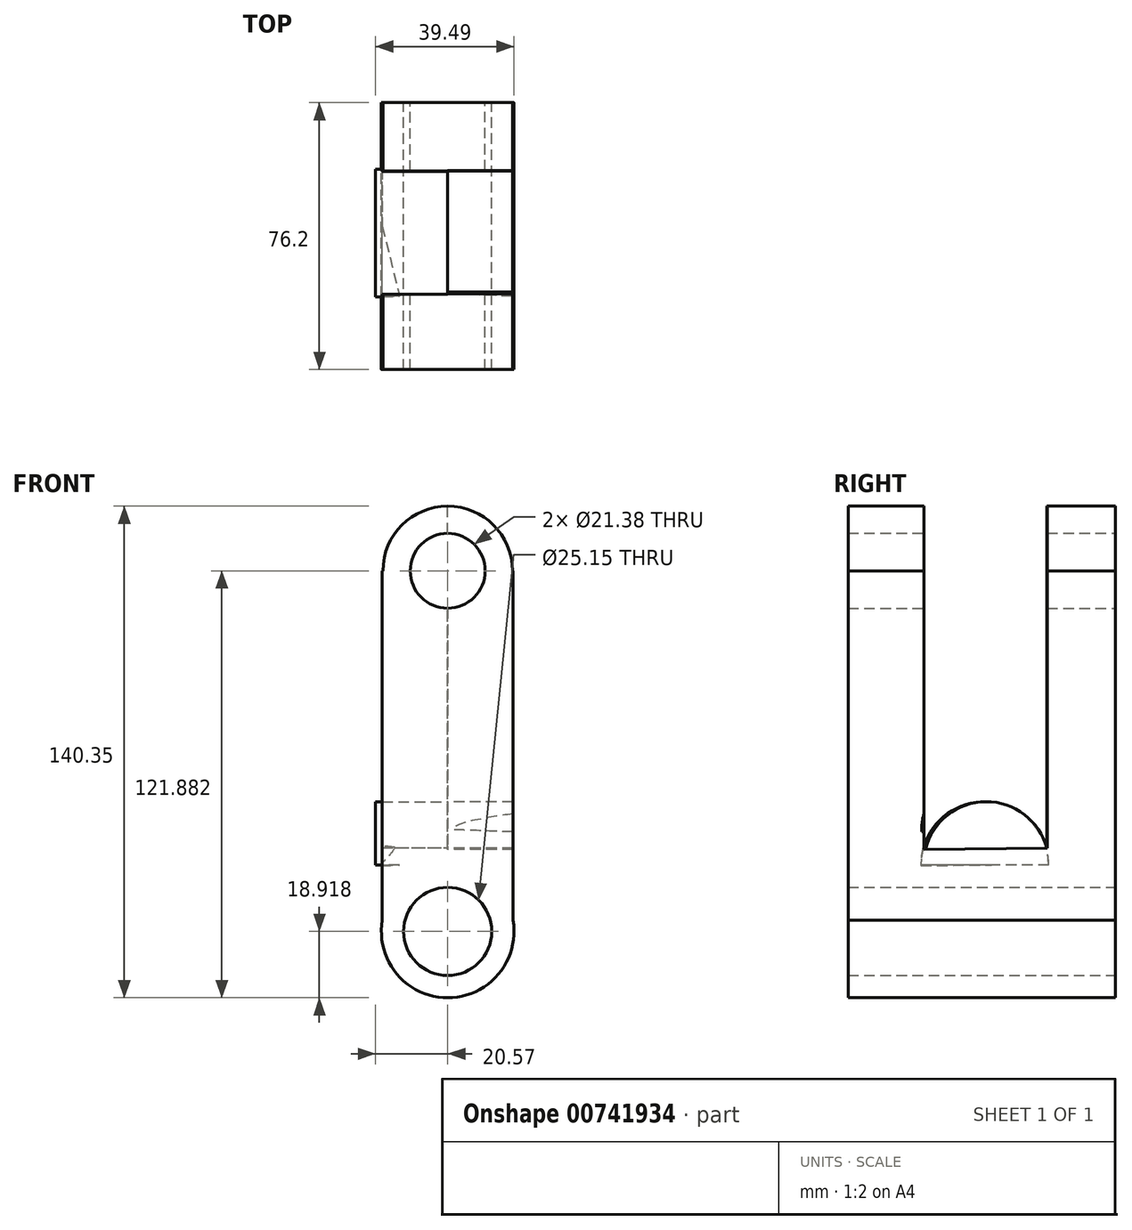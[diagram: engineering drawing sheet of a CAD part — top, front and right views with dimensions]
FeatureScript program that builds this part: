
annotation { "Feature Type Name" : "Feature", "Feature Type Description" : "" }
export const myFeature = defineFeature(function(context is Context, id is Id, definition is map)
    precondition{}
    {
        {
            var Q0;
            Q0=qCreatedBy(makeId("Front.planeOp"),FACE);
            var sketch = newSketch(context, id + "F0", { "sketchPlane" : qUnion([Q0])});
            skLineSegment(sketch, "E0.bottom", {"start": v(18.64, 51.48) * mm, "end": v(18.46, 51.48) * mm});
            skLineSegment(sketch, "E0.left", {"start": v(18.64, 51.48) * mm, "end": v(18.64, -51.48) * mm});
            skLineSegment(sketch, "E0.right", {"start": v(-18.64, 51.48) * mm, "end": v(-18.64, -51.48) * mm});
            skPoint(sketch, "E0.middle", {"position": v(0, 0) * mm});
            skArc(sketch, "E1", {"start": v(18.46, 51.48) * mm, "mid": v(0, 69.95) * mm, "end": v(-18.46, 51.48) * mm});
            skCircle(sketch, "E2", {"center": v(0, 51.48) * mm, "radius": 10.7 * mm});
            skArc(sketch, "E3", {"start": v(-18.64, -48.27) * mm, "mid": v(0, -70.4) * mm, "end": v(18.64, -48.27) * mm});
            skCircle(sketch, "E4", {"center": v(0, -51.48) * mm, "radius": 12.57 * mm});
            skLineSegment(sketch, "E5.trimOffspring", {"start": v(-18.46, 51.48) * mm, "end": v(-18.64, 51.48) * mm});
            skSolve(sketch);
        }
        {
            var Q0;
            {var subQ4=sQuery(id+"F0.wireOp",EDGE,"E0.bottom");Q0=makeQuery(id+"F0.imprint","IMPRINT",FACE,{"disambiguationData":[TD([[makeQuery(id+"F0.imprint","IMPRINT",EDGE,{"derivedFrom":subQ4}),1.0]])]});}
            extrude(context, id + "F1", {"entities" : qUnion([Q0]), "depth" : 76.2 * mm, "offsetDistance" : 25.4 * mm, "symmetric" : true});
        }
        {
            var Q0;
            Q0=qCreatedBy(makeId("Right.planeOp"),FACE);
            var sketch = newSketch(context, id + "F2", { "sketchPlane" : qUnion([Q0])});
            skArc(sketch, "E6", {"start": v(0, -15.34) * mm, "mid": v(11.68, -20.12) * mm, "end": v(16.65, -31.71) * mm});
            skArc(sketch, "E7", {"start": v(0, -15.34) * mm, "mid": v(-11.78, -20.22) * mm, "end": v(-16.66, -32) * mm});
            skLineSegment(sketch, "E8", {"start": v(16.65, -31.71) * mm, "end": v(-16.66, -32) * mm});
            skSolve(sketch);
        }
        {
            var Q0;
            Q0 = qSketchRegion(id + "F2", true);
            extrude(context, id + "F3", {"entities" : qUnion([Q0]), "operationType" : NewBodyOperationType.REMOVE, "oppositeDirection" : true, "depth" : 76.2 * mm, "offsetDistance" : 25.4 * mm, "hasDraft" : true, "draftAngle" : 2 * degree});
        }
        {
            var Q0;
            Q0=qCreatedBy(makeId("Right.planeOp"),FACE);
            var sketch = newSketch(context, id + "F4", { "sketchPlane" : qUnion([Q0])});
            skArc(sketch, "E9", {"start": v(0, -5.95) * mm, "mid": v(-11.61, -10.76) * mm, "end": v(-16.42, -22.38) * mm});
            skArc(sketch, "E10", {"start": v(0, -5.95) * mm, "mid": v(11.61, -10.76) * mm, "end": v(16.42, -22.38) * mm});
            skLineSegment(sketch, "E11", {"start": v(-16.42, -22.38) * mm, "end": v(16.42, -22.38) * mm});
            skSolve(sketch);
        }
        {
            var Q0;
            Q0 = qSketchRegion(id + "F4", true);
            extrude(context, id + "F5", {"entities" : qUnion([Q0]), "operationType" : NewBodyOperationType.REMOVE, "depth" : 76.2 * mm, "offsetDistance" : 25.4 * mm, "hasDraft" : true, "draftAngle" : 2 * degree});
        }
        {
            var Q0;
            Q0=qCreatedBy(makeId("Right.planeOp"),FACE);
            var sketch = newSketch(context, id + "F6", { "sketchPlane" : qUnion([Q0])});
            skLineSegment(sketch, "E12", {"start": v(-16.58, -27.52) * mm, "end": v(-16.58, 70.15) * mm});
            skLineSegment(sketch, "E13", {"start": v(-16.58, 70.15) * mm, "end": v(18.62, 70.15) * mm});
            skLineSegment(sketch, "E14", {"start": v(18.62, 70.15) * mm, "end": v(18.62, -27.52) * mm});
            skLineSegment(sketch, "E15", {"start": v(18.62, -27.52) * mm, "end": v(-16.58, -27.52) * mm});
            skSolve(sketch);
        }
        {
            var Q0;
            Q0 = qSketchRegion(id + "F6", true);
            extrude(context, id + "F7", {"entities" : qUnion([Q0]), "operationType" : NewBodyOperationType.REMOVE, "oppositeDirection" : true, "depth" : 76.2 * mm, "offsetDistance" : 25.4 * mm});
        }
        {
            var Q0;
            Q0=qCreatedBy(makeId("Right.planeOp"),FACE);
            var sketch = newSketch(context, id + "F8", { "sketchPlane" : qUnion([Q0])});
            skLineSegment(sketch, "E16", {"start": v(-16.47, -28) * mm, "end": v(-16.47, 70.08) * mm});
            skLineSegment(sketch, "E17", {"start": v(-16.47, 70.08) * mm, "end": v(18.71, 70.08) * mm});
            skLineSegment(sketch, "E18", {"start": v(18.71, 70.08) * mm, "end": v(18.71, -27.73) * mm});
            skLineSegment(sketch, "E19", {"start": v(18.71, -27.73) * mm, "end": v(-16.47, -28) * mm});
            skSolve(sketch);
        }
        {
            var Q0;
            Q0 = qSketchRegion(id + "F8", true);
            extrude(context, id + "F9", {"entities" : qUnion([Q0]), "operationType" : NewBodyOperationType.REMOVE, "depth" : 76.2 * mm, "offsetDistance" : 25.4 * mm});
        }
        {
            var Q0;
            Q0=qCreatedBy(makeId("Right.planeOp"),FACE);
            var sketch = newSketch(context, id + "F10", { "sketchPlane" : qUnion([Q0])});
            skArc(sketch, "E20", {"start": v(18.97, -29.4) * mm, "mid": v(1.1, -14.44) * mm, "end": v(-16.33, -29.9) * mm});
            skLineSegment(sketch, "E21", {"start": v(-16.33, -29.9) * mm, "end": v(18.97, -29.4) * mm});
            skSolve(sketch);
        }
        {
            var Q0;
            Q0 = qSketchRegion(id + "F10", true);
            extrude(context, id + "F11", {"entities" : qUnion([Q0]), "operationType" : NewBodyOperationType.ADD, "depth" : 18.54 * mm, "offsetDistance" : 25.4 * mm});
        }
        {
            var Q0;
            Q0=qCreatedBy(makeId("Right.planeOp"),FACE);
            var sketch = newSketch(context, id + "F12", { "sketchPlane" : qUnion([Q0])});
            skArc(sketch, "E22", {"start": v(19.13, -32.48) * mm, "mid": v(0.9, -14.43) * mm, "end": v(-17.32, -32.48) * mm});
            skLineSegment(sketch, "E23", {"start": v(19.13, -32.48) * mm, "end": v(-17.32, -32.48) * mm});
            skSolve(sketch);
        }
        {
            var Q0;
            Q0 = qSketchRegion(id + "F12", true);
            extrude(context, id + "F13", {"entities" : qUnion([Q0]), "operationType" : NewBodyOperationType.ADD, "oppositeDirection" : true, "depth" : 20.57 * mm, "offsetDistance" : 25.4 * mm});
        }
    });
